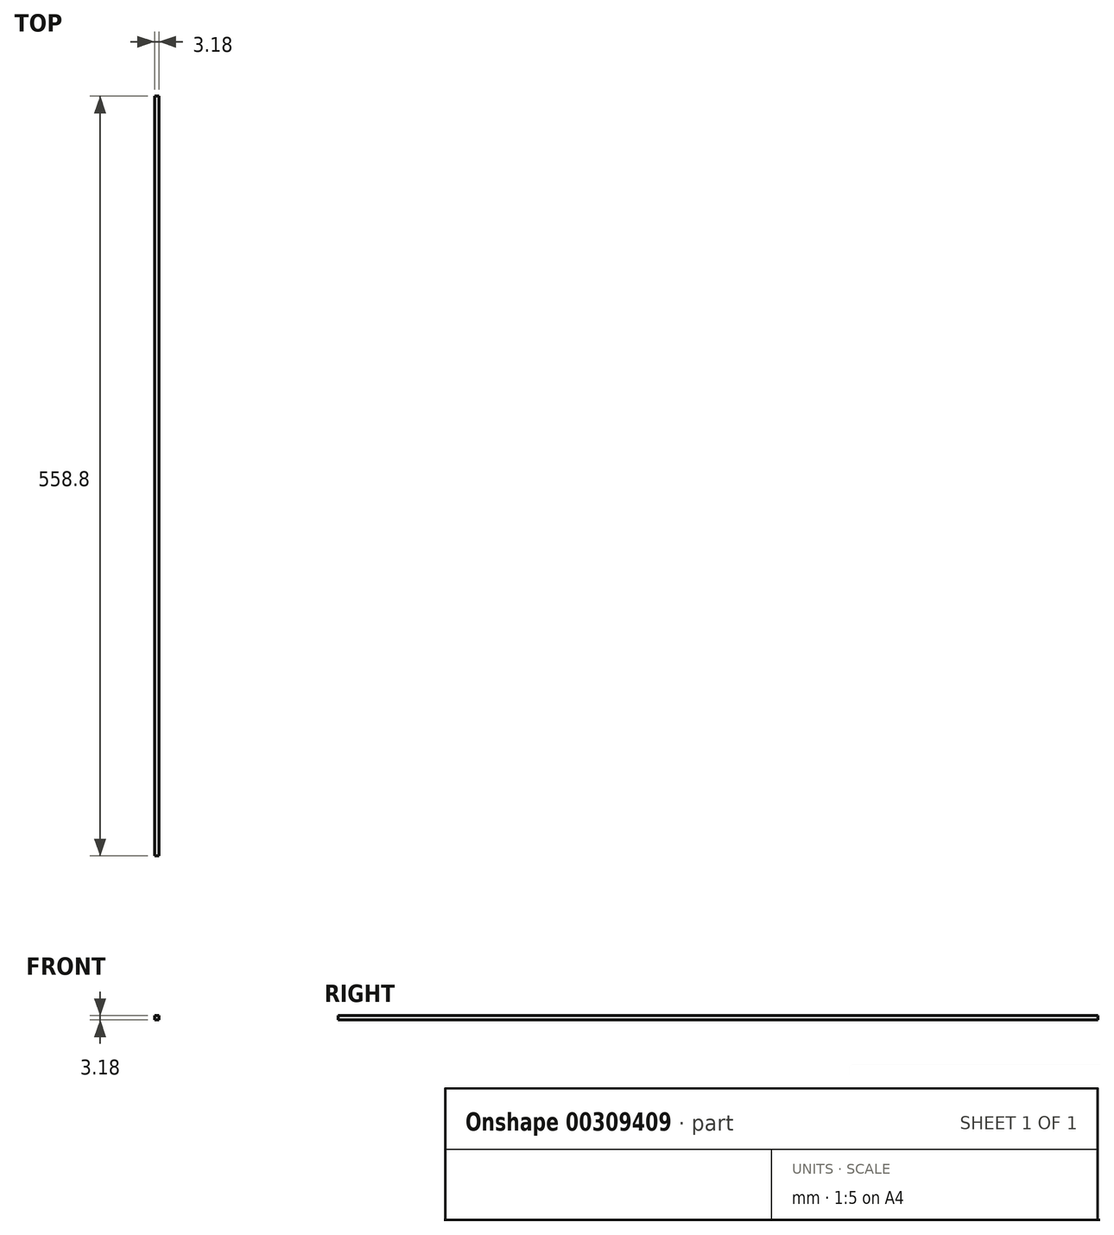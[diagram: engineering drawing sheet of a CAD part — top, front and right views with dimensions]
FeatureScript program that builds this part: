
annotation { "Feature Type Name" : "Feature", "Feature Type Description" : "" }
export const myFeature = defineFeature(function(context is Context, id is Id, definition is map)
    precondition{}
    {
        {
            var Q0;
            Q0=qCreatedBy(makeId("Front.planeOp"),FACE);
            var sketch = newSketch(context, id + "F0", { "sketchPlane" : qUnion([Q0])});
            skLineSegment(sketch, "E0.bottom", {"start": v(1.59, -1.59) * mm, "end": v(-1.59, -1.59) * mm});
            skLineSegment(sketch, "E0.top", {"start": v(1.59, 1.59) * mm, "end": v(-1.59, 1.59) * mm});
            skLineSegment(sketch, "E0.left", {"start": v(1.59, -1.59) * mm, "end": v(1.59, 1.59) * mm});
            skLineSegment(sketch, "E0.right", {"start": v(-1.59, -1.59) * mm, "end": v(-1.59, 1.59) * mm});
            skPoint(sketch, "E0.middle", {"position": v(0, 0) * mm});
            skSolve(sketch);
        }
        {
            var Q0;
            Q0=makeQuery(id+"F0.imprint","IMPRINT",FACE,{"disambiguationData":[TD([[makeQuery(id+"F0.imprint","IMPRINT",EDGE,{"derivedFrom":sQuery(id+"F0.wireOp",EDGE,"E0.bottom")}),-1.0]])]});
            extrude(context, id + "F1", {"entities" : qUnion([Q0]), "depth" : 558.8 * mm});
        }
    });
